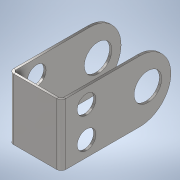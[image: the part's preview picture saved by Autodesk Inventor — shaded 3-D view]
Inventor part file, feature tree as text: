
AUTODESK INVENTOR PART (.ipt)
format: ipt  version: 2022 (Build 260153000, 153)  size: 214,016 bytes
history: native  units: mm
features: sheet_metal_op x3, sketch x2, other x2, extrude x1, fillet x1, projected_geometry x1
ambient origin geometry x8: Origin, YZ Plane, XZ Plane, XY Plane, X Axis, Y Axis, Z Axis, Center Point
bodies: Solid1 (feature_tree)
feature tree (10):
  sheet_metal_op  "Contour Flange1"
  extrude  "Extrusion1"  Depth=31.0mm
  fillet  "Fillet1"  Radius=70.0mm
  sketch  "Sketch1"  dims[d0=31.0mm d1=70.0mm d2=70.0mm]
  other  "Plate1"
  sheet_metal_op  "Bend1"
  sheet_metal_op  "Corner1"
  sketch  "Sketch2"  dims[d3=1.5mm d4=1.5mm d5=0.75mm d6=3.0mm d7=1.5mm d8=40.0mm d9=1.5mm d10=1.5mm d11=6.0mm d12=1.5mm d13=1.5mm d14=12.2mm d15=12.2mm d16=20.0mm d17=10.0mm d18=15.0mm d19=15.0mm d20=18.0mm d21=15.0mm d22=20.0mm d23=0.0mm d24=0.0mm d25=20.25mm]
  projected_geometry  "Projected Loop1"
  other  "Definition1"
